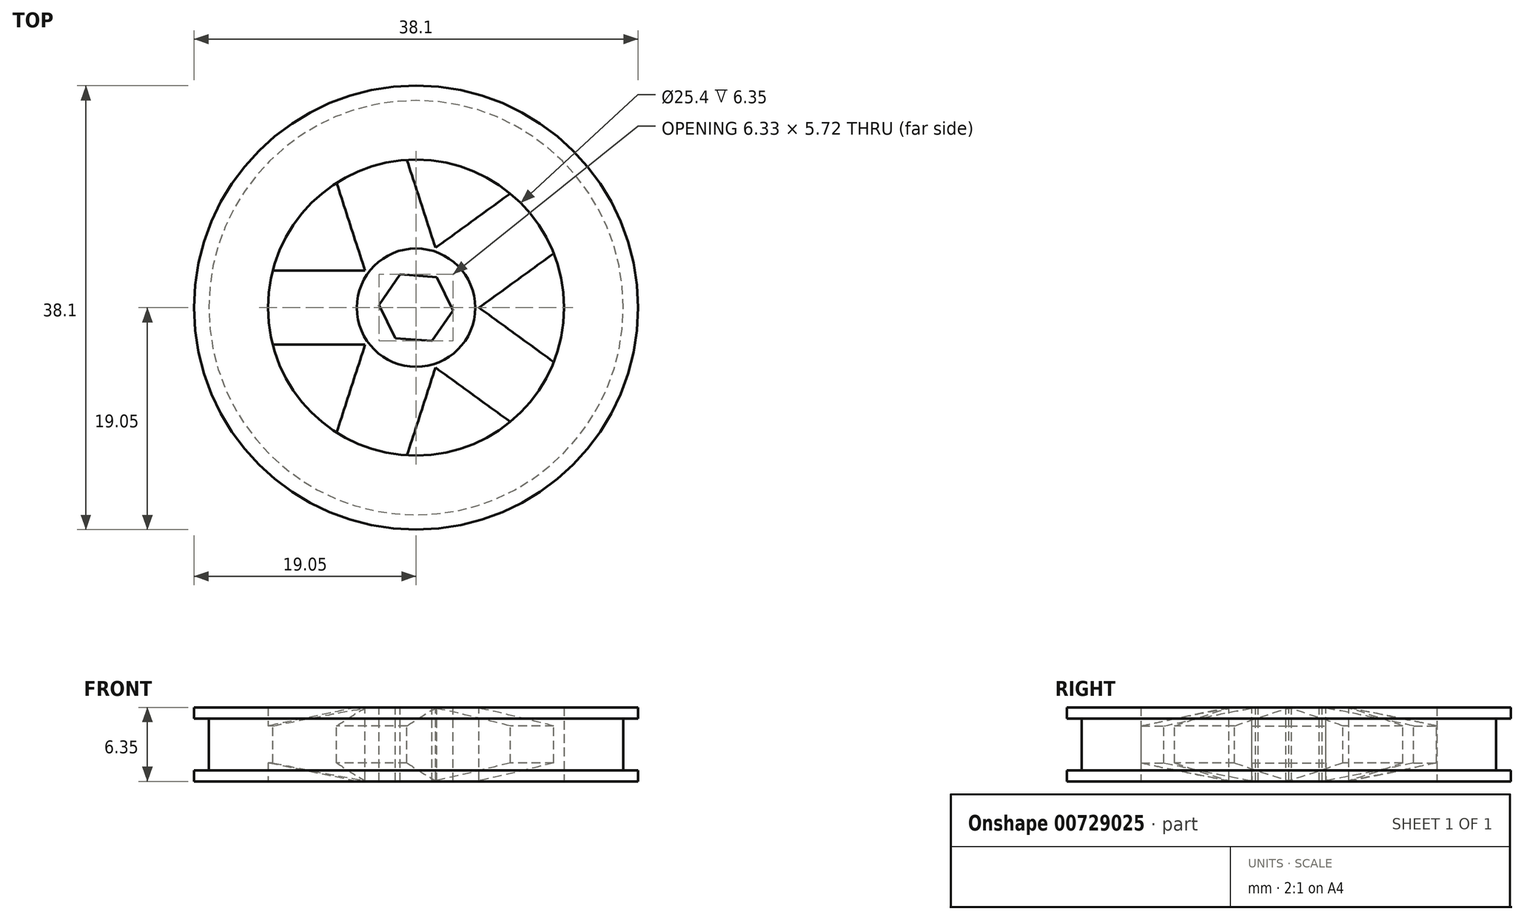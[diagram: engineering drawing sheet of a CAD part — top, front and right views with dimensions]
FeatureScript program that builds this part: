
annotation { "Feature Type Name" : "Feature", "Feature Type Description" : "" }
export const myFeature = defineFeature(function(context is Context, id is Id, definition is map)
    precondition{}
    {
        {
            var Q0;
            Q0=qCreatedBy(makeId("Front.planeOp"),FACE);
            var sketch = newSketch(context, id + "F0", { "sketchPlane" : qUnion([Q0])});
            skLineSegment(sketch, "E0.bottom", {"start": v(-28.82, 5.4) * mm, "end": v(-22.47, 5.4) * mm});
            skLineSegment(sketch, "E0.top", {"start": v(-28.82, -0.95) * mm, "end": v(-22.47, -0.95) * mm});
            skLineSegment(sketch, "E0.left", {"start": v(-28.82, 5.4) * mm, "end": v(-28.82, -0.95) * mm});
            skLineSegment(sketch, "E0.right", {"start": v(-22.47, 5.4) * mm, "end": v(-22.47, -0.95) * mm});
            skLineSegment(sketch, "E1", {"start": v(-22.47, 2.22) * mm, "end": v(-41.52, 2.22) * mm});
            skPoint(sketch, "E2", {"position": v(-38.35, 2.22) * mm});
            skLineSegment(sketch, "E3.bottom", {"start": v(-38.35, -0.95) * mm, "end": v(-36.44, -0.95) * mm});
            skLineSegment(sketch, "E3.top", {"start": v(-38.35, 5.4) * mm, "end": v(-36.44, 5.4) * mm});
            skLineSegment(sketch, "E3.left", {"start": v(-38.35, -0.95) * mm, "end": v(-38.35, 5.4) * mm});
            skLineSegment(sketch, "E3.right", {"start": v(-36.44, -0.95) * mm, "end": v(-36.44, 5.4) * mm});
            skLineSegment(sketch, "E4", {"start": v(-36.44, 3.81) * mm, "end": v(-28.82, 3.81) * mm});
            skLineSegment(sketch, "E5", {"start": v(-36.44, 0.64) * mm, "end": v(-28.82, 0.64) * mm});
            skLineSegment(sketch, "E6", {"start": v(-36.44, 5.4) * mm, "end": v(-28.82, 3.81) * mm});
            skLineSegment(sketch, "E7", {"start": v(-36.44, -0.95) * mm, "end": v(-28.82, 0.63) * mm});
            skLineSegment(sketch, "E8", {"start": v(-41.52, -14.99) * mm, "end": v(-41.52, 19.18) * mm});
            skLineSegment(sketch, "E9", {"start": v(-41.52, 2.22) * mm, "end": v(-60.57, 2.22) * mm});
            skLineSegment(sketch, "E10", {"start": v(-60.57, 4.45) * mm, "end": v(-60.57, 0) * mm});
            skLineSegment(sketch, "E11", {"start": v(-60.57, 4.45) * mm, "end": v(-59.3, 4.45) * mm});
            skLineSegment(sketch, "E12", {"start": v(-59.3, 4.45) * mm, "end": v(-59.3, 0) * mm});
            skLineSegment(sketch, "E13", {"start": v(-59.3, 0) * mm, "end": v(-60.57, 0) * mm});
            skSolve(sketch);
        }
        {
            var Q0;
            Q0 = qSketchRegion(id + "F0", true);
            var Q1;
            Q1=sQuery(id+"F0.wireOp",EDGE,"E8");
            revolve(context, id + "F1", {"surfaceOperationType" : NewSurfaceOperationType.NEW, "entities" : qUnion([Q0]), "axis" : qUnion([Q1]), "revolveType" : RevolveType.FULL});
        }
        {
            var Q0;
            Q0=makeQuery(id+"F1.opRevolve","SWEPT_FACE",FACE,{"disambiguationData":[OSD([sQuery(id+"F0.wireOp",EDGE,"E3.top")])]});
            var sketch = newSketch(context, id + "F2", { "sketchPlane" : qUnion([Q0])});
            skCircle(sketch, "E14.cCircle", {"center": v(-41.52, 0) * mm, "radius": 12.7 * mm, "construction": true});
            skLineSegment(sketch, "E14.0", {"start": v(-31.25, 7.46) * mm, "end": v(-31.25, -7.46) * mm});
            skLineSegment(sketch, "E14.1", {"start": v(-31.25, -7.46) * mm, "end": v(-45.44, -12.08) * mm});
            skLineSegment(sketch, "E14.2", {"start": v(-45.44, -12.08) * mm, "end": v(-54.22, 0) * mm});
            skLineSegment(sketch, "E14.3", {"start": v(-54.22, 0) * mm, "end": v(-45.44, 12.08) * mm});
            skLineSegment(sketch, "E14.4", {"start": v(-45.44, 12.08) * mm, "end": v(-31.25, 7.46) * mm});
            skLineSegment(sketch, "E15", {"start": v(-45.44, 12.08) * mm, "end": v(-41.52, 0) * mm});
            skLineSegment(sketch, "E16", {"start": v(-41.52, 0) * mm, "end": v(-31.25, 7.46) * mm});
            skLineSegment(sketch, "E17", {"start": v(-31.25, -7.46) * mm, "end": v(-41.52, 0) * mm});
            skLineSegment(sketch, "E18", {"start": v(-45.44, -12.08) * mm, "end": v(-41.52, 0) * mm});
            skLineSegment(sketch, "E19", {"start": v(-54.22, 0) * mm, "end": v(-41.52, 0) * mm});
            skLineSegment(sketch, "E20", {"start": v(-38.82, 1.96) * mm, "end": v(-46.67, 26.12) * mm});
            skLineSegment(sketch, "E21", {"start": v(-44.86, 0) * mm, "end": v(-53.13, 25.47) * mm});
            skLineSegment(sketch, "E22", {"start": v(-42.55, 3.17) * mm, "end": v(-23.63, 16.92) * mm});
            skLineSegment(sketch, "E23", {"start": v(-38.82, -1.96) * mm, "end": v(-19.38, 12.16) * mm});
            skLineSegment(sketch, "E24", {"start": v(-38.82, 1.96) * mm, "end": v(-17.59, -13.46) * mm});
            skLineSegment(sketch, "E25", {"start": v(-42.55, -3.17) * mm, "end": v(-20.83, -18.95) * mm});
            skLineSegment(sketch, "E26", {"start": v(-38.82, -1.96) * mm, "end": v(-46.86, -26.71) * mm});
            skLineSegment(sketch, "E27", {"start": v(-44.86, 0) * mm, "end": v(-53.31, -26.02) * mm});
            skLineSegment(sketch, "E28", {"start": v(-42.55, 3.17) * mm, "end": v(-68.13, 3.17) * mm});
            skLineSegment(sketch, "E29", {"start": v(-42.55, -3.17) * mm, "end": v(-68.29, -3.17) * mm});
            skCircle(sketch, "E30", {"center": v(-41.52, 0) * mm, "radius": 12.7 * mm});
            skCircle(sketch, "E31", {"center": v(-41.53, 0.1) * mm, "radius": 3.18 * mm});
            skLineSegment(sketch, "E32", {"start": v(-40.16, -2.77) * mm, "end": v(-38.37, -0.15) * mm});
            skLineSegment(sketch, "E33", {"start": v(-38.37, -0.15) * mm, "end": v(-39.74, 2.71) * mm});
            skLineSegment(sketch, "E34", {"start": v(-39.74, 2.71) * mm, "end": v(-42.9, 2.95) * mm});
            skLineSegment(sketch, "E35", {"start": v(-42.9, 2.95) * mm, "end": v(-44.7, 0.33) * mm});
            skLineSegment(sketch, "E36", {"start": v(-40.16, -2.77) * mm, "end": v(-43.33, -2.53) * mm});
            skLineSegment(sketch, "E37", {"start": v(-43.33, -2.53) * mm, "end": v(-44.7, 0.33) * mm});
            skSolve(sketch);
        }
        {
            var Q0;
            {var subQ0=sQuery(id+"F2.wireOp",EDGE,"E20");var subQ1=sQuery(id+"F2.wireOp",EDGE,"E14.4");var subQ2=makeQuery(id+"F2.imprint","INTERSECT",VERTEX,{"derivedFrom":[subQ1,subQ0]});Q0=makeQuery(id+"F2.imprint","IMPRINT",FACE,{"disambiguationData":[TD([[makeQuery(id+"F2.imprint","IMPRINT",EDGE,{"disambiguationData":[TD([[subQ2,-1.0]])],"derivedFrom":subQ1}),1.0]])]});}
            var Q1;
            {var subQ0=sQuery(id+"F2.wireOp",EDGE,"E20");var subQ1=sQuery(id+"F2.wireOp",EDGE,"E14.4");var subQ2=makeQuery(id+"F2.imprint","INTERSECT",VERTEX,{"derivedFrom":[subQ1,subQ0]});Q1=makeQuery(id+"F2.imprint","IMPRINT",FACE,{"disambiguationData":[TD([[makeQuery(id+"F2.imprint","IMPRINT",EDGE,{"disambiguationData":[TD([[subQ2,-1.0]])],"derivedFrom":subQ1}),-1.0]])]});}
            var Q2;
            {var subQ0=sQuery(id+"F2.wireOp",EDGE,"E28");var subQ1=sQuery(id+"F2.wireOp",EDGE,"E14.3");var subQ2=makeQuery(id+"F2.imprint","INTERSECT",VERTEX,{"derivedFrom":[subQ1,subQ0]});Q2=makeQuery(id+"F2.imprint","IMPRINT",FACE,{"disambiguationData":[TD([[makeQuery(id+"F2.imprint","IMPRINT",EDGE,{"disambiguationData":[TD([[subQ2,-1.0]])],"derivedFrom":subQ1}),1.0]])]});}
            var Q3;
            {var subQ0=sQuery(id+"F2.wireOp",EDGE,"E28");var subQ1=sQuery(id+"F2.wireOp",EDGE,"E14.3");var subQ2=makeQuery(id+"F2.imprint","INTERSECT",VERTEX,{"derivedFrom":[subQ1,subQ0]});Q3=makeQuery(id+"F2.imprint","IMPRINT",FACE,{"disambiguationData":[TD([[makeQuery(id+"F2.imprint","IMPRINT",EDGE,{"disambiguationData":[TD([[subQ2,-1.0]])],"derivedFrom":subQ1}),-1.0]])]});}
            var Q4;
            {var subQ0=sQuery(id+"F2.wireOp",EDGE,"E27");var subQ1=sQuery(id+"F2.wireOp",EDGE,"E14.2");var subQ2=makeQuery(id+"F2.imprint","INTERSECT",VERTEX,{"derivedFrom":[subQ1,subQ0]});Q4=makeQuery(id+"F2.imprint","IMPRINT",FACE,{"disambiguationData":[TD([[makeQuery(id+"F2.imprint","IMPRINT",EDGE,{"disambiguationData":[TD([[subQ2,-1.0]])],"derivedFrom":subQ1}),1.0]])]});}
            var Q5;
            {var subQ0=sQuery(id+"F2.wireOp",EDGE,"E27");var subQ1=sQuery(id+"F2.wireOp",EDGE,"E14.2");var subQ2=makeQuery(id+"F2.imprint","INTERSECT",VERTEX,{"derivedFrom":[subQ1,subQ0]});Q5=makeQuery(id+"F2.imprint","IMPRINT",FACE,{"disambiguationData":[TD([[makeQuery(id+"F2.imprint","IMPRINT",EDGE,{"disambiguationData":[TD([[subQ2,-1.0]])],"derivedFrom":subQ1}),-1.0]])]});}
            var Q6;
            {var subQ0=sQuery(id+"F2.wireOp",EDGE,"E25");var subQ1=sQuery(id+"F2.wireOp",EDGE,"E14.1");var subQ2=makeQuery(id+"F2.imprint","INTERSECT",VERTEX,{"derivedFrom":[subQ1,subQ0]});Q6=makeQuery(id+"F2.imprint","IMPRINT",FACE,{"disambiguationData":[TD([[makeQuery(id+"F2.imprint","IMPRINT",EDGE,{"disambiguationData":[TD([[subQ2,-1.0]])],"derivedFrom":subQ1}),-1.0]])]});}
            var Q7;
            {var subQ0=sQuery(id+"F2.wireOp",EDGE,"E25");var subQ1=sQuery(id+"F2.wireOp",EDGE,"E14.1");var subQ2=makeQuery(id+"F2.imprint","INTERSECT",VERTEX,{"derivedFrom":[subQ1,subQ0]});Q7=makeQuery(id+"F2.imprint","IMPRINT",FACE,{"disambiguationData":[TD([[makeQuery(id+"F2.imprint","IMPRINT",EDGE,{"disambiguationData":[TD([[subQ2,-1.0]])],"derivedFrom":subQ1}),1.0]])]});}
            var Q8;
            {var subQ0=sQuery(id+"F2.wireOp",EDGE,"E23");var subQ1=sQuery(id+"F2.wireOp",EDGE,"E14.0");var subQ2=makeQuery(id+"F2.imprint","INTERSECT",VERTEX,{"derivedFrom":[subQ1,subQ0]});Q8=makeQuery(id+"F2.imprint","IMPRINT",FACE,{"disambiguationData":[TD([[makeQuery(id+"F2.imprint","IMPRINT",EDGE,{"disambiguationData":[TD([[subQ2,-1.0]])],"derivedFrom":subQ1}),-1.0]])]});}
            var Q9;
            {var subQ0=sQuery(id+"F2.wireOp",EDGE,"E23");var subQ1=sQuery(id+"F2.wireOp",EDGE,"E14.0");var subQ2=makeQuery(id+"F2.imprint","INTERSECT",VERTEX,{"derivedFrom":[subQ1,subQ0]});Q9=makeQuery(id+"F2.imprint","IMPRINT",FACE,{"disambiguationData":[TD([[makeQuery(id+"F2.imprint","IMPRINT",EDGE,{"disambiguationData":[TD([[subQ2,-1.0]])],"derivedFrom":subQ1}),1.0]])]});}
            extrude(context, id + "F3", {"entities" : qUnion([Q0, Q1, Q2, Q3, Q4, Q5, Q6, Q7, Q8, Q9]), "operationType" : NewBodyOperationType.REMOVE, "oppositeDirection" : true, "depth" : 25.4 * mm, "offsetDistance" : 25.4 * mm});
        }
        {
            var Q0;
            {var subQ5=sQuery(id+"F0.wireOp",EDGE,"E11");Q0=makeQuery(id+"F0.imprint","IMPRINT",FACE,{"disambiguationData":[TD([[makeQuery(id+"F0.imprint","IMPRINT",EDGE,{"derivedFrom":subQ5}),-1.0]])]});}
            var Q1;
            {var subQ5=sQuery(id+"F0.wireOp",EDGE,"E13");Q1=makeQuery(id+"F0.imprint","IMPRINT",FACE,{"disambiguationData":[TD([[makeQuery(id+"F0.imprint","IMPRINT",EDGE,{"derivedFrom":subQ5}),-1.0]])]});}
            var Q2;
            Q2=sQuery(id+"F0.wireOp",EDGE,"E8");
            revolve(context, id + "F4", {"operationType" : NewBodyOperationType.REMOVE, "surfaceOperationType" : NewSurfaceOperationType.NEW, "entities" : qUnion([Q0, Q1]), "axis" : qUnion([Q2]), "revolveType" : RevolveType.FULL, "oppositeDirection" : true});
        }
        {
            var Q0;
            Q0=makeQuery(id+"F1.opRevolve","SWEPT_FACE",FACE,{"disambiguationData":[OSD([sQuery(id+"F0.wireOp",EDGE,"E3.top")])]});
            var sketch = newSketch(context, id + "F5", { "sketchPlane" : qUnion([Q0])});
            skCircle(sketch, "E38", {"center": v(-41.52, 0) * mm, "radius": 3.18 * mm});
            skLineSegment(sketch, "E39", {"start": v(-40.15, -2.86) * mm, "end": v(-38.35, -0.24) * mm});
            skLineSegment(sketch, "E40", {"start": v(-38.35, -0.24) * mm, "end": v(-39.73, 2.62) * mm});
            skLineSegment(sketch, "E41", {"start": v(-39.73, 2.62) * mm, "end": v(-42.9, 2.86) * mm});
            skLineSegment(sketch, "E42", {"start": v(-42.9, 2.86) * mm, "end": v(-44.69, 0.24) * mm});
            skLineSegment(sketch, "E43", {"start": v(-40.15, -2.86) * mm, "end": v(-43.31, -2.62) * mm});
            skLineSegment(sketch, "E44", {"start": v(-43.31, -2.62) * mm, "end": v(-44.69, 0.24) * mm});
            skSolve(sketch);
        }
        {
            var Q0;
            {var subQ0=sQuery(id+"F5.wireOp",EDGE,"E42");Q0=makeQuery(id+"F5.imprint","IMPRINT",FACE,{"disambiguationData":[TD([[makeQuery(id+"F5.imprint","IMPRINT",EDGE,{"derivedFrom":subQ0}),-1.0]])]});}
            var Q1;
            {var subQ0=sQuery(id+"F5.wireOp",EDGE,"E44");Q1=makeQuery(id+"F5.imprint","IMPRINT",FACE,{"disambiguationData":[TD([[makeQuery(id+"F5.imprint","IMPRINT",EDGE,{"derivedFrom":subQ0}),1.0]])]});}
            var Q2;
            {var subQ0=sQuery(id+"F5.wireOp",EDGE,"E43");Q2=makeQuery(id+"F5.imprint","IMPRINT",FACE,{"disambiguationData":[TD([[makeQuery(id+"F5.imprint","IMPRINT",EDGE,{"derivedFrom":subQ0}),1.0]])]});}
            var Q3;
            {var subQ0=sQuery(id+"F5.wireOp",EDGE,"E39");Q3=makeQuery(id+"F5.imprint","IMPRINT",FACE,{"disambiguationData":[TD([[makeQuery(id+"F5.imprint","IMPRINT",EDGE,{"derivedFrom":subQ0}),-1.0]])]});}
            var Q4;
            {var subQ0=sQuery(id+"F5.wireOp",EDGE,"E40");Q4=makeQuery(id+"F5.imprint","IMPRINT",FACE,{"disambiguationData":[TD([[makeQuery(id+"F5.imprint","IMPRINT",EDGE,{"derivedFrom":subQ0}),-1.0]])]});}
            var Q5;
            {var subQ0=sQuery(id+"F5.wireOp",EDGE,"E41");Q5=makeQuery(id+"F5.imprint","IMPRINT",FACE,{"disambiguationData":[TD([[makeQuery(id+"F5.imprint","IMPRINT",EDGE,{"derivedFrom":subQ0}),-1.0]])]});}
            extrude(context, id + "F6", {"entities" : qUnion([Q0, Q1, Q2, Q3, Q4, Q5]), "operationType" : NewBodyOperationType.ADD, "oppositeDirection" : true, "depth" : 6.35 * mm, "offsetDistance" : 25.4 * mm});
        }
    });
